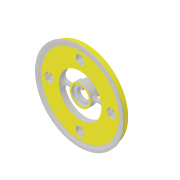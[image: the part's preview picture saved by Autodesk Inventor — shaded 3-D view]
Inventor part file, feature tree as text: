
AUTODESK INVENTOR PART (.ipt)
format: ipt  version: 2018 (Build 220112000, 112)  size: 669,184 bytes
history: native  units: in
note: dims shown in document units (in); Inventor stores cm internally (conversion verified against a paired STEP export)
features: sketch x14, extrude x13, fillet x8, pattern_circular x2, plane x1, mirror x1, revolve x1, projected_geometry x1
ambient origin geometry x8: Origin, YZ Plane, XZ Plane, XY Plane, X Axis, Y Axis, Z Axis, Center Point
bodies: Solid1 (feature_tree)
feature tree (41):
  extrude  "Extrusion1"  Depth=0.25in
  extrude  "Extrusion2"  Depth=0.65in
  extrude  "Extrusion3"  Depth=0.0394in
  extrude  "Extrusion4"  Depth=0.495in TaperAngle=0.0deg
  extrude  "Extrusion5"  Depth=0.0591in TaperAngle=0.0deg
  plane  "Work Plane1"
  extrude  "Extrusion6"  Depth=0.0394in TaperAngle=0.0deg
  mirror  "Mirror1"
  revolve  "Revolution1"  [1 undecoded]
  fillet  "Fillet1"  Radius=0.1908in
  extrude  "Extrusion8"  Depth=0.2756in
  fillet  "Fillet3"  Radius=0.6412in
  extrude  "Extrusion9"  Depth=0.2234in TaperAngle=0.0deg
  extrude  "Extrusion10"  Depth=0.0394in
  fillet  "Fillet4"  Radius=0.0394in
  fillet  "Fillet5"  Radius=0.0625in
  extrude  "Extrusion11"  Depth=0.125in
  fillet  "Fillet6"  Radius=1.5in
  extrude  "Extrusion12"  Depth=0.4125in
  extrude  "Extrusion13"  Depth=0.125in
  pattern_circular  "Circular Pattern2"  [2 undecoded]
  pattern_circular  "Circular Pattern3"  [2 undecoded]
  extrude  "Extrusion14"  Depth=0.1575in TaperAngle=0.0deg
  fillet  "Fillet7"  Radius=0.025in
  fillet  "Fillet8"  Radius=0.02in
  fillet  "Fillet9"  Radius=0.75in
  sketch  "Sketch1"  dims[d0=3.0in d2=0.25in]
  sketch  "Sketch2"  dims[d3=0.1969in d4=0.0in d7=0.65in]
  sketch  "Sketch3"  dims[d8=0.27in d9=0.0394in]
  sketch  "Sketch4"  dims[d10=0.0197in d11=0.495in d12=0.0in]
  sketch  "Sketch5"  dims[d13=0.0394in d14=0.0591in d15=0.0in]
  sketch  "Sketch6"  dims[d16=0.0394in d17=0.0in d18=0.0394in d19=0.0in]
  sketch  "Sketch7"  dims[d20=0.0866in d21=0.0954in d22=0.1908in]
  sketch  "Sketch9"  dims[d23=0.2672in d24=0.2756in d25=0.6412in d26=0.0in]
  sketch  "Sketch10"  dims[d27=-0.35in d29=0.2234in d30=0.0in]
  sketch  "Sketch11"  dims[d31=0.65in d32=0.0394in d33=0.0394in d34=0.0625in]
  projected_geometry  "Projected Loop1"
  sketch  "Sketch12"  dims[d35=90.0deg d36=0.125in d37=1.5in d38=0.75in]
  sketch  "Sketch13"  dims[d48=0.5344in d49=0.4125in]
  sketch  "Sketch14"  dims[d50=0.1969in d51=0.0in d52=0.125in]
  sketch  "Sketch15"  dims[d53=0.625in d54=0.2106in d55=0.0in d57=0.4134in d58=0.1181in d59=0.0in d60=0.025in d61=0.02in d62=0.75in d63=1.5in d64=0.0481in d65=1.0in d66=0.0in d67=0.125in d68=0.1772in d69=1.1in d70=1.1in d71=1.0in d72=0.0in d76=0.13in d78=0.1181in d79=0.0in d80=1.5748in d81=360.0deg d83=1.5748in d84=360.0deg d86=0.2953in d87=0.1654in d88=0.1181in d89=0.0in d90=0.125in d91=0.0512in d92=0.1575in]
note: 5 required parameter values undecoded (feature->parameter linkage not recoverable at this tier; creation-order binding heuristic only, values carry confidence <= 0.55)